# Revit family: Scrub_Sink-Infection_Control-American_Standard-ICS-IC-Everclean-9118_Series
name_source: partatom
category: Plumbing Fixtures
units: mm (PartAtom-declared; Revit-internal decimal feet)

## family parameters
Cut with Voids When Loaded = No
Host = Face
OmniClass Number = 23.45.05.14.14.21
OmniClass Title = Surgeons Scrub-Up Sinks
Part Type = Normal
Room Calculation Point = No
Round Connector Dimension = Use Diameter
Shared = Yes

## types (4) — shared parameters
7381266-200.0070A ICU Sink Bracket Assembly = No
7381267-400.0070A Mounting Kit = No
Assembly Code = D2010440
CW Connection = No
CWFU = 3
Cold Water Connection Diameter = 3/8"
Cold Water Connection Height = 20"
Cold Water Connection Width = 4"
Compliance Certifications = Meets or Exceeds ASME A112.19.2-2008 / CSA B45.1-08 for Vitreous China Fixtures
• CSA Z8000
Default Elevation = 34"
Finish = Vitreous China-American Standard-020-White
Flow Rate = 1.5 gpm/5.7 L/min
HW Connection = No
HWFU = 3
Height = 26 1/8"
Hot Water Connection Diameter = 3/8"
Hot Water Connection Width = 4"
Installation Type = Wall Mounted
Length = 20"
Manufacturer = American Standard
Material = Vitreous China-American Standard-020-White
Product Documentation Link = https://americanstandard.box.com
Product Page URL = https://www.americanstandard.ca
Revised Date = 11/16/2022
URL = https://www.americanstandard.ca
Vent Connection = No
WFU = 4
Waste Connection = Yes
Waste Connection Diameter = 1 1/4"
Waste Connection Height = 18"
Width = 17"

## per-type parameters (varying)
| type | AC power supply (M950169-0070A) | CR-P2 lithium battery | Description | Drain | Faucet Visibility | P-Trap | Selectronic ICU Faucet AC Powered | Selectronic ICU Faucet DC Powered |
| 9118111.020 | No | No | Infection Control Wall-Hung EverClean Sink with Shroud, A-M Drain and A-M P-Trap | Yes | No | Yes | No | No |
| 9118911.020 | No | No | ICU Sink and Shroud Less Drain and P-Trap | No | No | No | No | No |
| 9118DC.020 | No | Yes | ICU Sink System with DC Powered Hands-Free Faucet | Yes | Yes | Yes | No | Yes |
| 9118AC.020 | Yes | No | ICU Sink System with AC Powered Hands-Free Faucet | Yes | Yes | Yes | Yes | No |

note: column(s) folded — value = type name in every type: Model

## geometry (parser evidence)
native form markers: Sweep x5
no freeform markers — native parametric forms only
